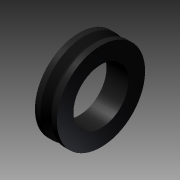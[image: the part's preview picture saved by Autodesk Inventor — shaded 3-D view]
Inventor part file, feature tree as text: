
AUTODESK INVENTOR PART (.ipt)
format: ipt  version: 2012 (Build 160160000, 160)  size: 104,960 bytes
history: native  units: in
note: dims shown in document units (in); Inventor stores cm internally (conversion verified against a paired STEP export)
features: revolve x1, sketch x1
ambient origin geometry x8: Origin, YZ Plane, XZ Plane, XY Plane, X Axis, Y Axis, Z Axis, Center Point
bodies: Solid1 (feature_tree)
feature tree (2):
  revolve  "Revolution1"  [1 undecoded]
  sketch  "Sketch1"  dims[d0=0.25in d1=0.1875in d2=0.0625in d3=0.3125in d5=0.4375in d6=0.375in d7=0.05in d8=0.0625in d9=0.1in d10=0.025in d11=90.0deg]
note: 1 required parameter value undecoded (feature->parameter linkage not recoverable at this tier; creation-order binding heuristic only, values carry confidence <= 0.55)
